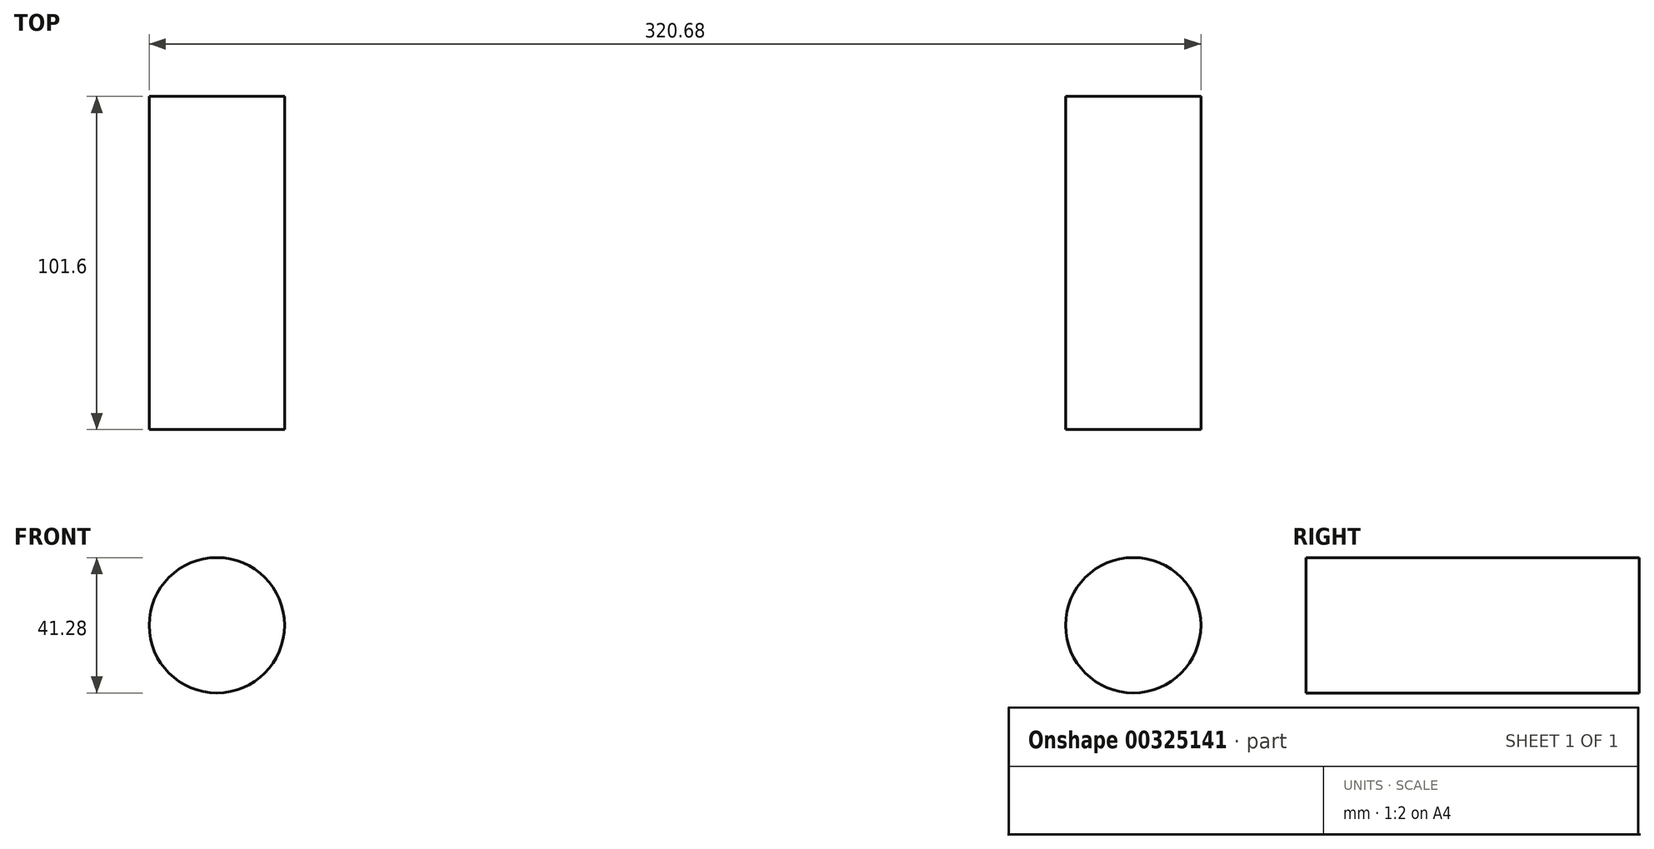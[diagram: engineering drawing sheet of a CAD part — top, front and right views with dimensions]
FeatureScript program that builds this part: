
annotation { "Feature Type Name" : "Feature", "Feature Type Description" : "" }
export const myFeature = defineFeature(function(context is Context, id is Id, definition is map)
    precondition{}
    {
        {
            var Q0;
            Q0=qCreatedBy(makeId("Top.planeOp"),FACE);
            var sketch = newSketch(context, id + "F0", { "sketchPlane" : qUnion([Q0])});
            skLineSegment(sketch, "E0", {"start": v(279.4, -101.6) * mm, "end": v(279.4, 0) * mm});
            skLineSegment(sketch, "E1", {"start": v(0, -101.6) * mm, "end": v(0, 0) * mm});
            skLineSegment(sketch, "E2.bottom", {"start": v(33.02, 67.89) * mm, "end": v(248.92, 67.89) * mm});
            skLineSegment(sketch, "E2.top", {"start": v(33.02, -114.3) * mm, "end": v(248.92, -114.3) * mm});
            skLineSegment(sketch, "E2.left", {"start": v(33.02, 67.89) * mm, "end": v(33.02, -114.3) * mm});
            skLineSegment(sketch, "E2.right", {"start": v(248.92, 67.89) * mm, "end": v(248.92, -114.3) * mm});
            skLineSegment(sketch, "E3.bottom", {"start": v(77.47, -381) * mm, "end": v(204.47, -381) * mm});
            skLineSegment(sketch, "E3.top", {"start": v(77.47, -549.3) * mm, "end": v(204.47, -549.3) * mm});
            skLineSegment(sketch, "E3.left", {"start": v(77.47, -381) * mm, "end": v(77.47, -549.3) * mm});
            skLineSegment(sketch, "E3.right", {"start": v(204.47, -381) * mm, "end": v(204.47, -549.3) * mm});
            skArc(sketch, "E4", {"start": v(279.4, -101.6) * mm, "mid": v(265.29, -141.51) * mm, "end": v(229.22, -163.69) * mm});
            skLineSegment(sketch, "E5", {"start": v(229.22, -163.69) * mm, "end": v(177.6, -174.76) * mm});
            skArc(sketch, "E6", {"start": v(177.6, -174.76) * mm, "mid": v(149.87, -188.4) * mm, "end": v(131.87, -213.51) * mm});
            skLineSegment(sketch, "E7", {"start": v(131.87, -213.51) * mm, "end": v(122.48, -237.27) * mm});
            skArc(sketch, "E8", {"start": v(122.48, -237.27) * mm, "mid": v(110.96, -256.03) * mm, "end": v(93.73, -269.74) * mm});
            skLineSegment(sketch, "E9", {"start": v(93.73, -269.74) * mm, "end": v(65.98, -284.81) * mm});
            skArc(sketch, "E10", {"start": v(65.98, -284.81) * mm, "mid": v(44.16, -304.35) * mm, "end": v(33.43, -331.6) * mm});
            skArc(sketch, "E11", {"start": v(0, -101.6) * mm, "mid": v(14.33, -141.79) * mm, "end": v(50.86, -163.83) * mm});
            skLineSegment(sketch, "E12", {"start": v(50.86, -163.83) * mm, "end": v(84, -170.56) * mm});
            skArc(sketch, "E13", {"start": v(84, -170.56) * mm, "mid": v(113.77, -185.53) * mm, "end": v(131.87, -213.51) * mm});
            skLineSegment(sketch, "E14", {"start": v(33.43, -331.6) * mm, "end": v(25.55, -386.58) * mm});
            skPoint(sketch, "E15", {"position": v(140.97, 67.89) * mm});
            skPoint(sketch, "E16", {"position": v(140.97, -549.3) * mm});
            skLineSegment(sketch, "E17.bottom", {"start": v(-19.05, 53.76) * mm, "end": v(19.05, 53.76) * mm});
            skLineSegment(sketch, "E17.top", {"start": v(-19.05, -50.8) * mm, "end": v(19.05, -50.8) * mm});
            skLineSegment(sketch, "E17.left", {"start": v(-19.05, 53.76) * mm, "end": v(-19.05, -50.8) * mm});
            skLineSegment(sketch, "E17.right", {"start": v(19.05, 53.76) * mm, "end": v(19.05, -50.8) * mm});
            skPoint(sketch, "E18", {"position": v(0, 53.76) * mm});
            skLineSegment(sketch, "E19.bottom", {"start": v(260.35, 52.8) * mm, "end": v(298.45, 52.8) * mm});
            skLineSegment(sketch, "E19.top", {"start": v(260.35, -38.1) * mm, "end": v(298.45, -38.1) * mm});
            skLineSegment(sketch, "E19.left", {"start": v(260.35, 52.8) * mm, "end": v(260.35, -38.1) * mm});
            skLineSegment(sketch, "E19.right", {"start": v(298.45, 52.8) * mm, "end": v(298.45, -38.1) * mm});
            skPoint(sketch, "E20", {"position": v(279.4, 52.8) * mm});
            skSolve(sketch);
        }
        {
            var Q0;
            Q0=qCreatedBy(makeId("Front.planeOp"),FACE);
            var sketch = newSketch(context, id + "F1", { "sketchPlane" : qUnion([Q0])});
            skCircle(sketch, "E21", {"center": v(279.4, 0) * mm, "radius": 20.64 * mm});
            skCircle(sketch, "E22", {"center": v(0, 0) * mm, "radius": 20.64 * mm});
            skSolve(sketch);
        }
        {
            var Q0;
            Q0 = qSketchRegion(id + "F1", true);
            var Q1;
            Q1=sQuery(id+"F1.wireOp",EDGE,"E21");
            var Q2;
            Q2=sQuery(id+"F0.wireOp",EDGE,"E0");
            sweep(context, id + "F2", {"bodyType" : ToolBodyType.SURFACE, "profiles" : qUnion([Q0]), "surfaceProfiles" : qUnion([Q1]), "path" : qUnion([Q2])});
        }
        {
            var Q0;
            Q0 = qSketchRegion(id + "F1", true);
            var Q1;
            Q1=sQuery(id+"F1.wireOp",EDGE,"E22");
            var Q2;
            Q2=sQuery(id+"F0.wireOp",EDGE,"E1");
            sweep(context, id + "F3", {"bodyType" : ToolBodyType.SURFACE, "profiles" : qUnion([Q0]), "surfaceProfiles" : qUnion([Q1]), "path" : qUnion([Q2])});
        }
    });
